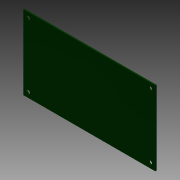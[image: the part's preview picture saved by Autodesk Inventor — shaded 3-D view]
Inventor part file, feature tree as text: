
AUTODESK INVENTOR PART (.ipt)
format: ipt  version: 2013 (Build 170138000, 138)  size: 124,416 bytes
history: native  units: in
note: dims shown in document units (in); Inventor stores cm internally (conversion verified against a paired STEP export)
features: extrude x2, sketch x2
ambient origin geometry x8: Origin, YZ Plane, XZ Plane, XY Plane, X Axis, Y Axis, Z Axis, Center Point
bodies: Solid1 (feature_tree)
feature tree (4):
  extrude  "Extrusion1"  Depth=4.0in
  extrude  "Extrusion3"  Depth=1.95in
  sketch  "Sketch1"  dims[d0=0.0394in d1=0.0in d2=4.0in]
  sketch  "Sketch3"  dims[d4=2.25in d5=1.95in d6=0.1102in d8=0.1102in d10=1.95in d15=0.0787in d16=0.1969in d17=0.1969in d18=0.0394in d19=0.1181in d20=0.0in d21=0.15in d22=0.15in d23=0.15in d24=0.15in d25=0.15in d26=0.15in d27=0.15in d28=0.15in d29=0.8in d30=2.1in d31=1.95in d32=3.7in d33=1.1469in d34=1.1469in]
